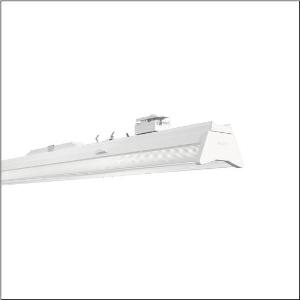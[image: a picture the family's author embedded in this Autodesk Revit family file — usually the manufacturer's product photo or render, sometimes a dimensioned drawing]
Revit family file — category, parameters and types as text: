
# Revit family: licross_r__11_performance_mo_51td16dn445g_6250
name_source: partatom
category: Lighting Fixtures
units: mm (PartAtom-declared; Revit-internal decimal feet)

## family parameters
Cut with Voids When Loaded = No
Host = Face
Light Source = No
Part Type = Normal
Room Calculation Point = No
Round Connector Dimension = Use Diameter
Shared = No

## types (1)
- --- (1 x LED, 4520 lm, 24.3 W, 4000K)
    Apparent Load = 24 VA
    CIE Flux Codes = 66 88 96 79 100
    Color Rendering = 80
    Color Temperature = 4000K
    Default Elevation = 1800 mm
    Description = Licross® 11 Performance MO, luminaire insert, of sheet steel, galvanised, coil coated, white, length: 1.500mm, width: 120mm, height: 123mm, LED rated luminous flux: 4.520lm, light colour: 840, control gear: DALI 2, with plug, 5-pole, with phase selection, mains connection: 220..240V, AC, 50/60Hz, rated input power: 24W, halogen-free wiring, primary light control with lens, of plastic, primary optical cover: cover, of PMMA, CAT 2 (L<= 3000cd/m²), light emission: direct/indirect distribution, primary light characteristic: symmetric, protection rating (complete): IP54, insulation class (complete): insulation class I (protective earthing), certification: CE, ENEC, VDE, UKCA, protection symbol: D if used in an environment with non-conductive dust loads with corresponding accessories, impact resistance: IK06, permissible ambient temperature for indoor applications: -25..+45°C, corresponds to IFS (International Featured Standards) requirements for safety and quality in the food industry, reducing of maximum allowable ambient temperature of 5°C with ceiling mounting, LABS conformity tested according to VDMA 24364:2018-05, packaging unit: 1 piece
    Height = 114 mm
    Lamp = 1 x LED
    Lamp Light Flux = 4520 lm
    Lamp Power = 24.3 W
    Lamp count = 1
    Length = 1500 mm
    Luminous efficacy = 186 lm/W
    Manufacturer = Siteco
    ModVariant = No
    Model = 51TD16DN445G
    Mounting Place = Ceiling
    Mounting Type = Pendant
    Number of Poles = 1
    OnlyDefault = Yes
    Power Factor = 1
    Product Name = Licross® 11 Performance MO
    Product group = luminaire insert
    ProductGroupID = 901
    Protection Class = Protection class I
    Protection Degree = IP 54
    RLX_Detail_Level = 1
    RLX_Emergency_Light_Flux = 0 lm
    RLX_Emergency_Type = 0
    RLX_Emergency_Type_DB = No
    RlxData = <blob elided: 33769 chars, md5=e3829c77>
    Socket = socket
    Standby Power = 0 W
    System Light Flux = 4520 lm
    System Power = 24 W
    Type Comments = factory setting: luminous flux: 100 % | dim-lin: 254 | 161 mA
    Type Image = l_1256138.jpg
    URL = http://relux.com
    VarID = @adj_031869
    Voltage = 0 V
    Weight = 0.00 kg
    Width = 120 mm

## geometry (parser evidence)
native form markers: Blend x4, Sweep x12
no freeform markers — native parametric forms only
